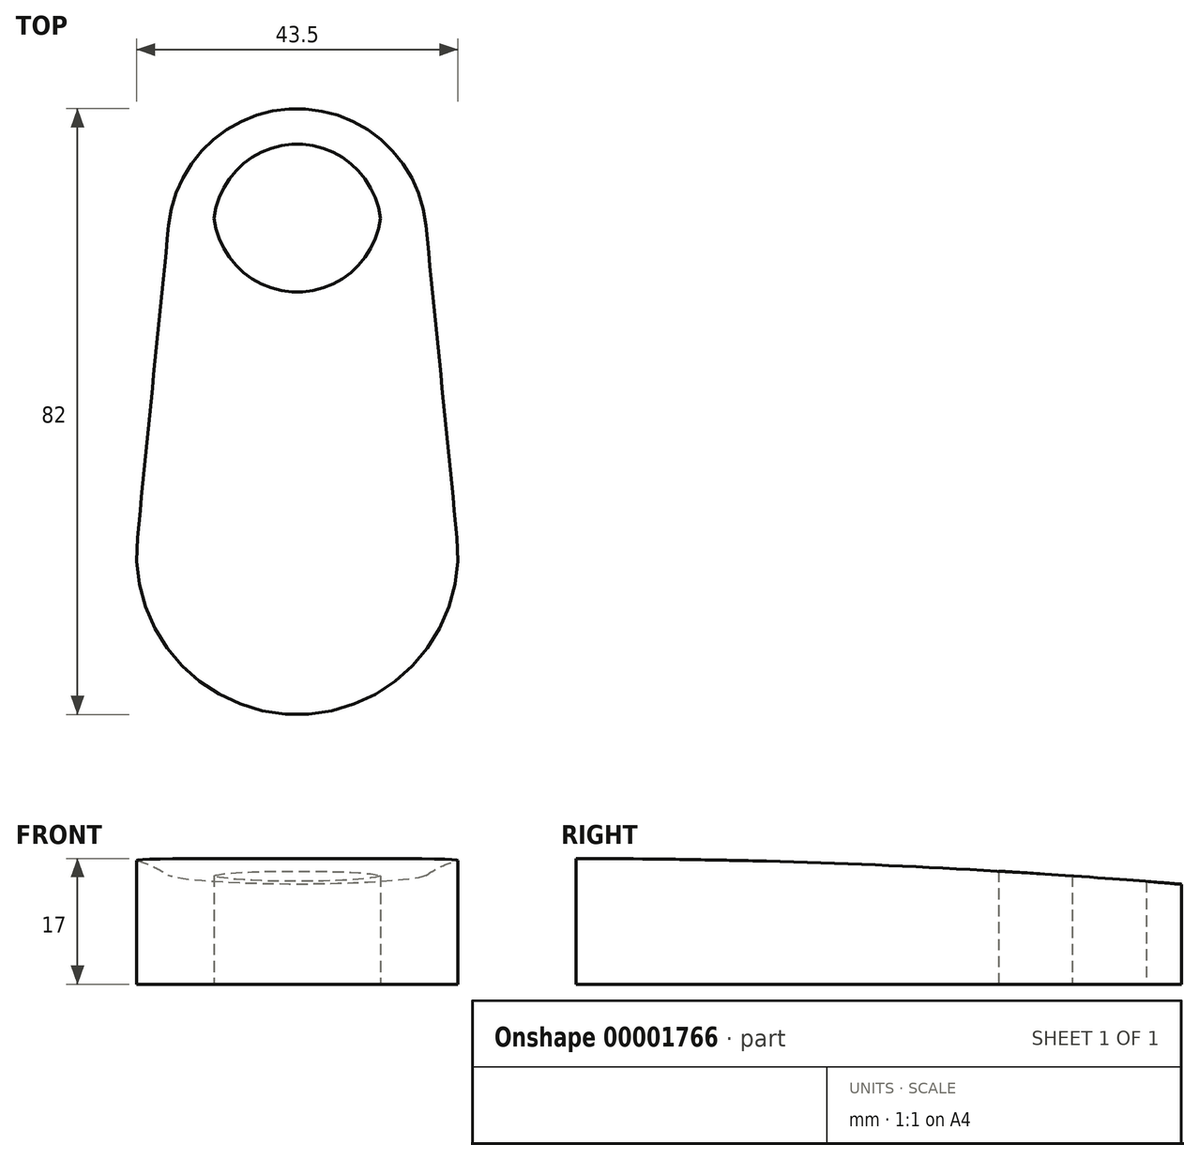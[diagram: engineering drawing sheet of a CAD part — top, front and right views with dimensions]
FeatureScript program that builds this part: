
annotation { "Feature Type Name" : "Feature", "Feature Type Description" : "" }
export const myFeature = defineFeature(function(context is Context, id is Id, definition is map)
    precondition{}
    {
        {
            var Q0;
            Q0=qCreatedBy(makeId("Top.planeOp"),FACE);
            var sketch = newSketch(context, id + "F0", { "sketchPlane" : qUnion([Q0])});
            skArc(sketch, "E0", {"start": v(17.41, 44.49) * mm, "mid": v(0, 60.25) * mm, "end": v(-17.41, 44.49) * mm});
            skArc(sketch, "E1", {"start": v(-21.64, 2.16) * mm, "mid": v(0, -21.75) * mm, "end": v(21.64, 2.16) * mm});
            skLineSegment(sketch, "E2", {"start": v(-21.64, 2.16) * mm, "end": v(-17.41, 44.49) * mm});
            skLineSegment(sketch, "E3", {"start": v(17.41, 44.49) * mm, "end": v(21.64, 2.16) * mm});
            skArc(sketch, "E4", {"start": v(11.25, 45.45) * mm, "mid": v(0, 55.45) * mm, "end": v(-11.25, 45.45) * mm});
            skArc(sketch, "E5", {"start": v(-11.25, 45.45) * mm, "mid": v(0, 35.45) * mm, "end": v(11.25, 45.45) * mm});
            skSolve(sketch);
        }
        {
            var Q0;
            Q0 = qSketchRegion(id + "F0", true);
            extrude(context, id + "F1", {"entities" : qUnion([Q0]), "endBound" : BoundingType.SYMMETRIC, "depth" : 17 * mm});
        }
        {
            var Q0;
            Q0=qCreatedBy(makeId("Right.planeOp"),FACE);
            var sketch = newSketch(context, id + "F2", { "sketchPlane" : qUnion([Q0])});
            skLineSegment(sketch, "E6", {"start": v(-22.34, 8.5) * mm, "end": v(60.5, 8.5) * mm});
            skLineSegment(sketch, "E7", {"start": v(60.5, 8.5) * mm, "end": v(60.5, 5) * mm});
            skArc(sketch, "E8", {"start": v(60.5, 5) * mm, "mid": v(19.12, 7.62) * mm, "end": v(-22.34, 8.5) * mm});
            skLineSegment(sketch, "E9", {"start": v(67.47, 8.5) * mm, "end": v(67.47, -25.63) * mm, "construction": true});
            skSolve(sketch);
        }
        {
            var Q0;
            Q0 = qSketchRegion(id + "F2", true);
            extrude(context, id + "F3", {"entities" : qUnion([Q0]), "operationType" : NewBodyOperationType.REMOVE, "endBound" : BoundingType.SYMMETRIC, "oppositeDirection" : true, "depth" : 100 * mm});
        }
    });
